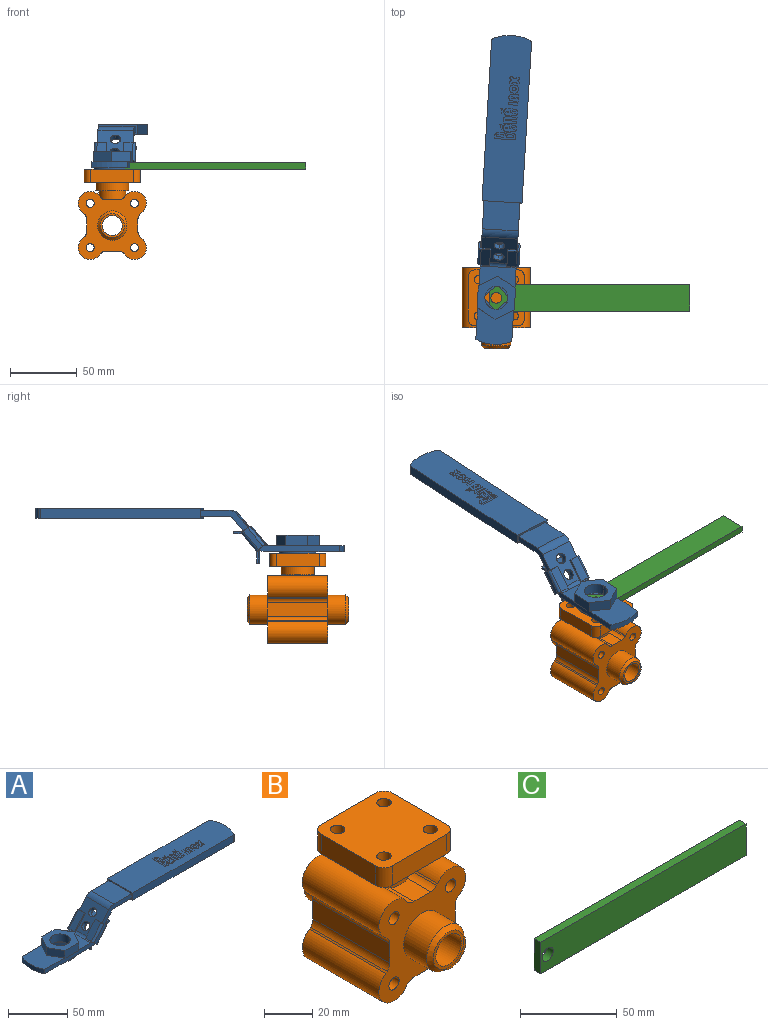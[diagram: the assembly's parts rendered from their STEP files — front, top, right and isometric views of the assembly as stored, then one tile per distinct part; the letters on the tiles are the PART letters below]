
ASSEMBLY  parts=3 mates=2
PART A: 211 faces, bbox 232x31x41.1 mm
  f0: plane 1.5x0.5mm, normal (-0.95,-0.32,0), area 0.2mm2, adj f1,f2,f4,f5
  f1: plane 125x30mm, normal (0,0,1), area 3406.6mm2, adj f0,f2,f3,f4,f6,f7,f8,f9
  f2: plane 3x0.5mm, normal (-0.16,0.99,0), area 0.3mm2, adj f0,f1,f3,f5
  f3: plane 1x0.5mm, normal (0.89,0.45,0), area 0.1mm2, adj f1,f2,f4,f5
  f4: plane 3x1mm, normal (0.32,-0.95,0), area 0.3mm2, adj f0,f1,f3,f5
  f5: plane 3.5x2mm, normal (0,0,1), area 4.1mm2, adj f0,f2,f3,f4
  f6: plane 3x0.5mm, normal (-0.16,0.99,0), area 0.3mm2, adj f1,f7,f9,f10
  f7: plane 1x0.5mm, normal (0.89,0.45,0), area 0.1mm2, adj f1,f6,f8,f10
  f8: plane 3x1mm, normal (0.32,-0.95,0), area 0.3mm2, adj f1,f7,f9,f10
  f9: plane 1.5x0.5mm, normal (-0.95,-0.32,0), area 0.2mm2, adj f1,f6,f8,f10
  f10: plane 3.5x2mm, normal (0,0,1), area 4.1mm2, adj f6,f7,f8,f9
  f11: cylinder r=3.04mm len=6mm, axis (0,0,1), area 0.9mm2, adj f1,f12,f14,f15
  f12: plane 1.86x0.1mm, normal (1,0,0), area 0.2mm2, adj f1,f11,f13,f15
  f13: cylinder r=3.04mm len=6mm, axis (0,0,1), area 0.9mm2, adj f1,f12,f14,f15
  f14: plane 1.86x0.1mm, normal (-1,0,0), area 0.2mm2, adj f1,f11,f13,f15
  f15: plane 7x6mm, normal (0,0,1), area 28.3mm2, adj f11,f12,f13,f14,f16,f17,f18,f19
  f16: plane 0.92x0.1mm, normal (-1,0,0), area 0.1mm2, adj f15,f17,f19,f20
  f17: cylinder r=1.27mm len=2.5mm, axis (0,0,1), area 0.4mm2, adj f15,f16,f18,f20
  f18: plane 0.92x0.1mm, normal (1,0,0), area 0.1mm2, adj f15,f17,f19,f20
  f19: cylinder r=1.27mm len=2.5mm, axis (0,0,1), area 0.4mm2, adj f15,f16,f18,f20
  f20: plane 3x2.5mm, normal (0,0,1), area 6.2mm2, adj f16,f17,f18,f19
  f21: plane 2x0.1mm, normal (0,1,0), area 0.2mm2, adj f1,f22,f30,f31
  f22: plane 4.7x0.1mm, normal (1,0,0), area 0.5mm2, adj f1,f21,f23,f31
  f23: cylinder r=2.3mm len=2.3mm, axis (0,0,1), area 0.4mm2, adj f1,f22,f24,f31
  f24: plane 0.4x0.1mm, normal (0,-1,0), area 0mm2, adj f1,f23,f25,f31
  f25: cylinder r=2.3mm len=2.3mm, axis (0,0,1), area 0.4mm2, adj f1,f24,f26,f31
  f26: plane 4.7x0.1mm, normal (-1,0,0), area 0.5mm2, adj f1,f25,f27,f31
  f27: plane 2x0.1mm, normal (0,1,0), area 0.2mm2, adj f1,f26,f28,f31
  f28: plane 5x0.1mm, normal (1,0,0), area 0.5mm2, adj f1,f27,f29,f31
  f29: plane 1x0.1mm, normal (0,1,0), area 0.1mm2, adj f1,f28,f30,f31
  f30: plane 5x0.1mm, normal (-1,0,0), area 0.5mm2, adj f1,f21,f29,f31
  f31: plane 7x5mm, normal (0,0,1), area 27.7mm2, adj f21,f22,f23,f24,f25,f26,f27,f28
  f32: plane 2x0.1mm, normal (0,1,0), area 0.2mm2, adj f1,f33,f35,f36
  f33: plane 7x0.1mm, normal (1,0,0), area 0.7mm2, adj f1,f32,f34,f36
  f34: plane 2x0.1mm, normal (0,-1,0), area 0.2mm2, adj f1,f33,f35,f36
  f35: plane 7x0.1mm, normal (-1,0,0), area 0.7mm2, adj f1,f32,f34,f36
  f36: plane 7x2mm, normal (0,0,1), area 14mm2, adj f32,f33,f34,f35
  f37: plane 2x0.1mm, normal (0,1,0), area 0.2mm2, adj f1,f38,f46,f47
  f38: plane 10x0.1mm, normal (1,0,0), area 1mm2, adj f1,f37,f39,f47
  f39: plane 2x0.1mm, normal (0,-1,0), area 0.2mm2, adj f1,f38,f40,f47
  f40: plane 0.27x0.1mm, normal (-1,0,0), area 0mm2, adj f1,f39,f41,f47
  f41: cylinder r=2mm len=3mm, axis (0,0,1), area 0.4mm2, adj f1,f40,f42,f47
  f42: plane 8x0.1mm, normal (-1,0,0), area 0.8mm2, adj f1,f41,f43,f47
  f43: plane 2x0.1mm, normal (0,1,0), area 0.2mm2, adj f1,f42,f44,f47
  f44: plane 8.5x0.1mm, normal (1,0,0), area 0.9mm2, adj f1,f43,f45,f47
  f45: plane 1x0.1mm, normal (0,1,0), area 0.1mm2, adj f1,f44,f46,f47
  f46: plane 8.5x0.1mm, normal (-1,0,0), area 0.9mm2, adj f1,f37,f45,f47
  f47: plane 10x5mm, normal (0,0,1), area 40.6mm2, adj f37,f38,f39,f40,f41,f42,f43,f44
  f48: cylinder r=2mm len=7.5mm, axis (0,0,1), area 17.3mm2, adj f1,f49,f134,f135
  f49: cylinder r=33.89mm len=27.63mm, axis (0,0,1), area 213.4mm2, adj f1,f48,f50,f135
  f50: cylinder r=2mm len=7.5mm, axis (0,0,1), area 17.3mm2, adj f1,f49,f51,f135
  f51: plane 120.23x7.5mm, normal (0,-1,0), area 901.7mm2, adj f1,f50,f52,f135
  f52: plane 30x7.5mm, normal (-1,0,0), area 103.5mm2, adj f1,f51,f53,f81,f105,f123,f134,f135
  f53: plane 104.03x31mm, normal (0,-1,0), area 520.7mm2, adj f52,f54,f56,f58,f59,f82,f100,f101
  f54: plane 27x22.22mm, normal (-0.77,0,0.64), area 671.8mm2, adj f53,f55,f56,f57,f58,f80,f81,f106
  f55: plane 14.49x12.72mm, normal (0,-1,0), area 26.8mm2, adj f54,f56,f59,f72,f80,f127
  f56: cylinder r=4mm len=27mm, axis (0,-1,0), area 68.6mm2, adj f53,f54,f55,f57,f59,f81,f82
  f57: plane 14.49x12.72mm, normal (0,1,0), area 26.8mm2, adj f54,f56,f58,f59,f72,f76
  f58: plane 13.79x11.57mm, normal (0.77,0,-0.64), area 117.3mm2, adj f53,f54,f57,f59,f72,f77
  f59: plane 31x6.13mm, normal (-0.64,0,-0.77), area 59.9mm2, adj f53,f55,f56,f57,f58,f60,f61,f65
  f60: cylinder r=3mm len=15mm, axis (0,-1,0), area 14.6mm2, adj f59,f61,f64,f65
  f61: plane 9.88x1.85mm, normal (0,-1,0), area 14.2mm2, adj f59,f60,f62,f63,f64,f66,f67
  f62: plane 15x8.91mm, normal (1,0,0), area 133.7mm2, adj f61,f63,f65,f66
  f63: plane 15x1.5mm, normal (0,0,-1), area 22.5mm2, adj f61,f62,f64,f65
  f64: plane 15x8.91mm, normal (-1,0,0), area 133.7mm2, adj f60,f61,f63,f65
  f65: plane 9.88x1.85mm, normal (0,1,0), area 14.2mm2, adj f59,f60,f62,f63,f64,f66,f67
  f66: cylinder r=1.5mm len=15mm, axis (0,-1,0), area 15.7mm2, adj f61,f62,f65,f67
  f67: plane 27x13.79mm, normal (0.77,0,-0.64), area 371.7mm2, adj f59,f61,f65,f66,f68,f70,f72,f73
  f68: cylinder r=1.5mm len=24.5mm, axis (0,-1,0), area 32.1mm2, adj f67,f69,f70,f131
  f69: plane 24.5x5.6mm, normal (0,0,-1), area 137.3mm2, adj f68,f70,f131,f132
  f70: plane 6.75x2.04mm, normal (0,-1,0), area 9.4mm2, adj f67,f68,f69,f71,f72,f132,f133
  f71: cylinder r=3mm len=24.5mm, axis (0,-1,0), area 28.5mm2, adj f70,f72,f131,f133
  f72: plane 31x6.13mm, normal (0.64,0,0.77), area 56.8mm2, adj f55,f57,f58,f67,f70,f71,f73,f74
  f73: cylinder r=2mm len=15.07mm, axis (0.64,0,0.77), area 56.5mm2, adj f59,f67,f72,f74
  f74: plane 16.36x14.63mm, normal (0,-1,0), area 72mm2, adj f59,f72,f73,f75
  f75: cylinder r=2mm len=15.07mm, axis (0.64,0,0.77), area 56.5mm2, adj f59,f72,f74,f76
  f76: plane 13.79x11.57mm, normal (-0.77,0,0.64), area 126mm2, adj f57,f59,f72,f75
  f77: plane 17x15.4mm, normal (0,1,0), area 90mm2, adj f58,f59,f72,f78
  f78: plane 28x13.79mm, normal (-0.77,0,0.64), area 440.4mm2, adj f59,f72,f77,f79,f125,f126
  f79: plane 17x15.4mm, normal (0,-1,0), area 90mm2, adj f59,f72,f78,f80
  f80: plane 13.79x11.57mm, normal (0.77,0,-0.64), area 117.3mm2, adj f54,f55,f59,f72,f79,f81
  f81: plane 104.03x31mm, normal (0,1,0), area 520.7mm2, adj f52,f54,f56,f59,f80,f82,f101,f102
  f82: plane 27x14.76mm, normal (0,0,1), area 293.3mm2, adj f53,f56,f81,f83,f84
  f83: plane 14x8.08mm, normal (0.87,0.5,0), area 129.3mm2, adj f82,f84,f88,f89,f121
  f84: plane 14x8.08mm, normal (0.87,-0.5,0), area 129.3mm2, adj f82,f83,f85,f89,f122
  f85: plane 16.17x8mm, normal (0,-1,0), area 129.3mm2, adj f84,f86,f89,f122
  f86: plane 14x8.08mm, normal (-0.87,-0.5,0), area 129.3mm2, adj f85,f87,f89,f113,f122
  f87: plane 14x8.08mm, normal (-0.87,0.5,0), area 129.3mm2, adj f86,f88,f89,f113,f121
  f88: plane 16.17x8mm, normal (0,1,0), area 129.3mm2, adj f83,f87,f89,f121
  f89: plane 32.33x28mm, normal (0,0,1), area 444.2mm2, adj f83,f84,f85,f86,f87,f88,f90,f91
  f90: cylinder r=8.64mm len=17.18mm, axis (0,0,1), area 217.3mm2, adj f89,f91,f114,f115,f117,f118
  f91: cylinder r=8.64mm len=17.18mm, axis (0,0,1), area 217.3mm2, adj f89,f90,f92,f116,f119,f120
  f92: plane 2.73x1.36mm, normal (0,0,-1), area 1.7mm2, adj f91,f93,f94
  f93: plane 9.9x9.9mm, normal (-0.71,-0.71,0), area 77mm2, adj f92,f94,f96,f97,f116,f120
  f94: plane 9.9x9.9mm, normal (-0.71,0.71,0), area 77mm2, adj f92,f93,f95,f97,f117,f119
  f95: plane 9.9x9.9mm, normal (0.71,0.71,0), area 77mm2, adj f94,f96,f97,f114,f117,f118
  f96: plane 9.9x9.9mm, normal (0.71,-0.71,0), area 77mm2, adj f93,f95,f97,f114,f115,f116
  f97: plane 28x28mm, normal (0,0,-1), area 419.8mm2, adj f93,f94,f95,f96,f98,f99
  f98: cylinder r=14mm len=28mm, axis (0,0,1), area 44mm2, adj f97,f99,f100,f110,f111
  f99: cylinder r=14mm len=28mm, axis (0,0,1), area 44mm2, adj f97,f98,f100,f101,f110
  f100: plane 7.42x0.5mm, normal (0,0,1), area 2.5mm2, adj f53,f98,f99
  f101: plane 27x19.66mm, normal (0,0,-1), area 325.6mm2, adj f53,f81,f99,f102
  f102: cylinder r=8mm len=27mm, axis (0,-1,0), area 188.5mm2, adj f53,f81,f101,f103
  f103: plane 27x22.21mm, normal (0.77,0,-0.64), area 682.4mm2, adj f53,f81,f102,f104,f106,f107,f108,f109
  f104: cylinder r=4mm len=27mm, axis (0,-1,0), area 94.3mm2, adj f53,f81,f103,f105
  f105: plane 27x20.82mm, normal (0,0,-1), area 562.1mm2, adj f52,f53,f81,f104
  f106: cylinder r=4mm len=9.02mm, axis (-0.77,0,0.64), area 56.6mm2, adj f54,f103,f107
  f107: cylinder r=4mm len=9.02mm, axis (-0.77,0,0.64), area 56.6mm2, adj f54,f103,f106
  f108: cylinder r=4mm len=9.02mm, axis (-0.77,0,0.64), area 56.5mm2, adj f54,f103,f109
  f109: cylinder r=4mm len=9.02mm, axis (-0.77,0,0.64), area 56.5mm2, adj f54,f103,f108
  f110: plane 7.42x0.5mm, normal (0,0,1), area 2.5mm2, adj f81,f98,f99
  f111: plane 31.3x27mm, normal (0,0,-1), area 613.4mm2, adj f53,f81,f98,f112
  f112: cylinder r=31.88mm len=27mm, axis (0,0,1), area 125.5mm2, adj f53,f81,f111,f113
  f113: plane 27x26.64mm, normal (0,0,1), area 587.5mm2, adj f53,f81,f86,f87,f112
  f114: plane 2.73x1.36mm, normal (0,0,-1), area 1.7mm2, adj f90,f95,f96
  f115: plane 7.17x7.17mm, normal (0,0,1), area 11.4mm2, adj f90,f96
  f116: plane 2.73x1.36mm, normal (0,0,-1), area 1.7mm2, adj f91,f93,f96
  f117: plane 2.73x1.36mm, normal (0,0,-1), area 1.7mm2, adj f90,f94,f95
  f118: plane 7.17x7.17mm, normal (0,0,1), area 11.4mm2, adj f90,f95
  f119: plane 7.17x7.17mm, normal (0,0,1), area 11.4mm2, adj f91,f94
  f120: plane 7.17x7.17mm, normal (0,0,1), area 11.4mm2, adj f91,f93
  f121: plane 16.74x0.5mm, normal (0,0,-1), area 8.2mm2, adj f81,f83,f87,f88
  f122: plane 16.74x0.5mm, normal (0,0,-1), area 8.2mm2, adj f53,f84,f85,f86
  f123: plane 27x21.05mm, normal (0,0,1), area 568.3mm2, adj f52,f53,f81,f124
  f124: cylinder r=8mm len=27mm, axis (0,-1,0), area 188.4mm2, adj f53,f54,f81,f123
  f125: cylinder r=4.5mm len=7.86mm, axis (-0.77,0,0.64), area 21.2mm2, adj f67,f78,f126
  f126: cylinder r=4.5mm len=7.86mm, axis (-0.77,0,0.64), area 21.2mm2, adj f67,f78,f125
  f127: plane 13.79x11.57mm, normal (-0.77,0,0.64), area 126mm2, adj f55,f59,f72,f128
  f128: cylinder r=2mm len=15.07mm, axis (0.64,0,0.77), area 56.5mm2, adj f59,f72,f127,f129
  f129: plane 16.36x14.63mm, normal (0,1,0), area 72mm2, adj f59,f72,f128,f130
  f130: cylinder r=2mm len=15.07mm, axis (0.64,0,0.77), area 56.5mm2, adj f59,f67,f72,f129
  f131: plane 6.75x2.04mm, normal (0,1,0), area 9.4mm2, adj f67,f68,f69,f71,f72,f132,f133
  f132: plane 24.5x1.5mm, normal (1,0,0), area 36.7mm2, adj f69,f70,f131,f133
  f133: plane 24.5x5.6mm, normal (0,0,1), area 137.3mm2, adj f70,f71,f131,f132
  f134: plane 120.23x7.5mm, normal (0,1,0), area 901.7mm2, adj f1,f48,f52,f135
  f135: plane 125x30mm, normal (0,0,-1), area 3715.2mm2, adj f48,f49,f50,f51,f52,f134
  f136: plane 2x0.1mm, normal (0,1,0), area 0.2mm2, adj f1,f137,f144,f145
  f137: plane 16x0.1mm, normal (1,0,0), area 1.6mm2, adj f1,f136,f138,f145
  f138: plane 2x0.1mm, normal (0,-1,0), area 0.2mm2, adj f1,f137,f139,f145
  f139: cylinder r=3mm len=3mm, axis (0,0,1), area 0.5mm2, adj f1,f138,f140,f145
  f140: plane 3x0.1mm, normal (-1,0,0), area 0.3mm2, adj f1,f139,f141,f145
  f141: cylinder r=2mm len=2mm, axis (0,0,1), area 0.3mm2, adj f1,f140,f142,f145
  f142: cylinder r=2mm len=2mm, axis (0,0,1), area 0.3mm2, adj f1,f141,f143,f145
  f143: plane 3x0.1mm, normal (-1,0,0), area 0.3mm2, adj f1,f142,f144,f145
  f144: cylinder r=3mm len=3mm, axis (0,0,1), area 0.5mm2, adj f1,f136,f143,f145
  f145: plane 16x5mm, normal (0,0,1), area 53.8mm2, adj f136,f137,f138,f139,f140,f141,f142,f143
  f146: plane 1x0.1mm, normal (0,-1,0), area 0.1mm2, adj f145,f147,f151,f152
  f147: cylinder r=1mm len=1mm, axis (0,0,1), area 0.2mm2, adj f145,f146,f148,f152
  f148: plane 3x0.1mm, normal (1,0,0), area 0.3mm2, adj f145,f147,f149,f152
  f149: cylinder r=1.5mm len=1.5mm, axis (0,0,1), area 0.2mm2, adj f145,f148,f150,f152
  f150: plane 0.5x0.1mm, normal (0,1,0), area 0.1mm2, adj f145,f149,f151,f152
  f151: plane 5.5x0.1mm, normal (-1,0,0), area 0.6mm2, adj f145,f146,f150,f152
  f152: plane 5.5x2mm, normal (0,0,1), area 10.3mm2, adj f146,f147,f148,f149,f150,f151
  f153: plane 5.5x0.1mm, normal (-1,0,0), area 0.6mm2, adj f145,f154,f158,f159
  f154: plane 0.5x0.1mm, normal (0,-1,0), area 0.1mm2, adj f145,f153,f155,f159
  f155: cylinder r=1.5mm len=1.5mm, axis (0,0,1), area 0.2mm2, adj f145,f154,f156,f159
  f156: plane 3x0.1mm, normal (1,0,0), area 0.3mm2, adj f145,f155,f157,f159
  f157: cylinder r=1mm len=1mm, axis (0,0,1), area 0.2mm2, adj f145,f156,f158,f159
  f158: plane 1x0.1mm, normal (0,1,0), area 0.1mm2, adj f145,f153,f157,f159
  f159: plane 5.5x2mm, normal (0,0,1), area 10.3mm2, adj f153,f154,f155,f156,f157,f158
  f160: plane 1x0.1mm, normal (0,1,0), area 0.1mm2, adj f1,f161,f173,f174
  f161: cylinder r=2mm len=2mm, axis (0,0,1), area 0.3mm2, adj f1,f160,f162,f174
  f162: plane 6x0.1mm, normal (1,0,0), area 0.6mm2, adj f1,f161,f163,f174
  f163: cylinder r=2mm len=2mm, axis (0,0,1), area 0.3mm2, adj f1,f162,f164,f174
  f164: plane 1x0.1mm, normal (0,-1,0), area 0.1mm2, adj f1,f163,f165,f174
  f165: cylinder r=2mm len=2mm, axis (0,0,1), area 0.3mm2, adj f1,f164,f166,f174
  f166: plane 3x0.1mm, normal (-1,0,0), area 0.3mm2, adj f1,f165,f167,f174
  f167: plane 3x0.1mm, normal (0,1,0), area 0.3mm2, adj f1,f166,f168,f174
  f168: plane 3.5x0.1mm, normal (-1,0,0), area 0.4mm2, adj f1,f167,f169,f174
  f169: plane 1x0.1mm, normal (0,-1,0), area 0.1mm2, adj f1,f168,f170,f174
  f170: plane 2.5x0.1mm, normal (1,0,0), area 0.3mm2, adj f1,f169,f171,f174
  f171: plane 2x0.1mm, normal (0,-1,0), area 0.2mm2, adj f1,f170,f172,f174
  f172: plane 2x0.1mm, normal (-1,0,0), area 0.2mm2, adj f1,f171,f173,f174
  f173: cylinder r=2mm len=2mm, axis (0,0,1), area 0.3mm2, adj f1,f160,f172,f174
  f174: plane 10x5mm, normal (0,0,1), area 39.1mm2, adj f160,f161,f162,f163,f164,f165,f166,f167
  f175: plane 2x0.1mm, normal (-1,0,0), area 0.2mm2, adj f174,f176,f178,f179
  f176: plane 1x0.1mm, normal (0,-1,0), area 0.1mm2, adj f174,f175,f177,f179
  f177: plane 2x0.1mm, normal (1,0,0), area 0.2mm2, adj f174,f176,f178,f179
  f178: plane 1x0.1mm, normal (0,1,0), area 0.1mm2, adj f174,f175,f177,f179
  f179: plane 2x1mm, normal (0,0,1), area 2mm2, adj f175,f176,f177,f178
  f180: plane 1x0.1mm, normal (0,1,0), area 0.1mm2, adj f1,f181,f193,f194
  f181: cylinder r=2mm len=2mm, axis (0,0,1), area 0.3mm2, adj f1,f180,f182,f194
  f182: plane 6x0.1mm, normal (1,0,0), area 0.6mm2, adj f1,f181,f183,f194
  f183: cylinder r=2mm len=2mm, axis (0,0,1), area 0.3mm2, adj f1,f182,f184,f194
  f184: plane 1x0.1mm, normal (0,-1,0), area 0.1mm2, adj f1,f183,f185,f194
  f185: cylinder r=2mm len=2mm, axis (0,0,1), area 0.3mm2, adj f1,f184,f186,f194
  f186: plane 3x0.1mm, normal (-1,0,0), area 0.3mm2, adj f1,f185,f187,f194
  f187: plane 3x0.1mm, normal (0,1,0), area 0.3mm2, adj f1,f186,f188,f194
  f188: plane 3.5x0.1mm, normal (-1,0,0), area 0.4mm2, adj f1,f187,f189,f194
  f189: plane 1x0.1mm, normal (0,-1,0), area 0.1mm2, adj f1,f188,f190,f194
  f190: plane 2.5x0.1mm, normal (1,0,0), area 0.3mm2, adj f1,f189,f191,f194
  f191: plane 2x0.1mm, normal (0,-1,0), area 0.2mm2, adj f1,f190,f192,f194
  f192: plane 2x0.1mm, normal (-1,0,0), area 0.2mm2, adj f1,f191,f193,f194
  f193: cylinder r=2mm len=2mm, axis (0,0,1), area 0.3mm2, adj f1,f180,f192,f194
  f194: plane 10x5mm, normal (0,0,1), area 39.1mm2, adj f180,f181,f182,f183,f184,f185,f186,f187
  f195: plane 2x0.1mm, normal (-1,0,0), area 0.2mm2, adj f194,f196,f198,f199
  f196: plane 1x0.1mm, normal (0,-1,0), area 0.1mm2, adj f194,f195,f197,f199
  f197: plane 2x0.1mm, normal (1,0,0), area 0.2mm2, adj f194,f196,f198,f199
  f198: plane 1x0.1mm, normal (0,1,0), area 0.1mm2, adj f194,f195,f197,f199
  f199: plane 2x1mm, normal (0,0,1), area 2mm2, adj f195,f196,f197,f198
  f200: plane 2x0.1mm, normal (1,0,0), area 0.2mm2, adj f1,f201,f209,f210
  f201: cylinder r=1.53mm len=3mm, axis (0,0,1), area 0.4mm2, adj f1,f200,f202,f210
  f202: plane 2.01x0.1mm, normal (1,0,0), area 0.2mm2, adj f1,f201,f203,f210
  f203: cylinder r=1.99mm len=2.5mm, axis (0,0,1), area 0.3mm2, adj f1,f202,f204,f210
  f204: cylinder r=1.99mm len=2.5mm, axis (0,0,1), area 0.3mm2, adj f1,f203,f205,f210
  f205: plane 2.01x0.1mm, normal (-1,0,0), area 0.2mm2, adj f1,f204,f206,f210
  f206: cylinder r=1.53mm len=3mm, axis (0,0,1), area 0.4mm2, adj f1,f205,f207,f210
  f207: plane 2x0.1mm, normal (-1,0,0), area 0.2mm2, adj f1,f206,f208,f210
  f208: cylinder r=1.99mm len=2.5mm, axis (0,0,1), area 0.3mm2, adj f1,f207,f209,f210
  f209: cylinder r=1.99mm len=2.5mm, axis (0,0,1), area 0.3mm2, adj f1,f200,f208,f210
  f210: plane 7.16x5mm, normal (0,0,1), area 27mm2, adj f200,f201,f202,f203,f204,f205,f206,f207
PART B: 59 faces, bbox 51x76x67.8 mm
  f0: plane 18.39x0.67mm, normal (0.71,0,0.71), area 15.9mm2, adj f1,f9,f28,f42
  f1: cylinder r=8.88mm len=45mm, axis (0,1,0), area 1425.9mm2, adj f0,f10,f11,f27,f28,f42
  f2: cylinder r=8.88mm len=45mm, axis (0,1,0), area 1425.9mm2, adj f3,f21,f22,f27,f28,f42
  f3: plane 18.39x0.67mm, normal (-0.71,0,0.71), area 15.9mm2, adj f2,f6,f28,f42
  f4: plane 13.8x9.86mm, normal (0,0,1), area 127.4mm2, adj f6,f9,f28,f42
  f5: plane 13.8x9.86mm, normal (0,0,1), area 127.4mm2, adj f7,f8,f27,f42
  f6: cylinder r=5mm len=17.18mm, axis (0,-1,0), area 60.1mm2, adj f3,f4,f28,f42
  f7: cylinder r=5mm len=17.18mm, axis (0,-1,0), area 60.1mm2, adj f5,f22,f27,f42
  f8: cylinder r=5mm len=17.18mm, axis (0,1,0), area 60.1mm2, adj f5,f10,f27,f42
  f9: cylinder r=5mm len=17.18mm, axis (0,1,0), area 60.1mm2, adj f0,f4,f28,f42
  f10: plane 18.39x0.67mm, normal (0.71,0,0.71), area 15.9mm2, adj f1,f8,f27,f42
  f11: plane 45x0.64mm, normal (-0.71,0,-0.71), area 40.4mm2, adj f1,f27,f28,f29
  f12: plane 45x9.86mm, normal (-1,0,0), area 443.6mm2, adj f27,f28,f29,f30
  f13: plane 45x0.64mm, normal (-0.71,0,0.71), area 40.4mm2, adj f14,f27,f28,f30
  f14: cylinder r=8.88mm len=45mm, axis (0,1,0), area 1434.5mm2, adj f13,f15,f27,f28
  f15: plane 45x0.64mm, normal (0.71,0,-0.71), area 40.4mm2, adj f14,f27,f28,f31
  f16: plane 45x9.86mm, normal (0,0,-1), area 443.6mm2, adj f27,f28,f31,f32
  f17: plane 45x0.64mm, normal (-0.71,0,-0.71), area 40.4mm2, adj f18,f27,f28,f32
  f18: cylinder r=8.88mm len=45mm, axis (0,1,0), area 1434.5mm2, adj f17,f19,f27,f28
  f19: plane 45x0.64mm, normal (0.71,0,0.71), area 40.4mm2, adj f18,f27,f28,f33
  f20: plane 45x9.86mm, normal (1,0,0), area 443.6mm2, adj f27,f28,f33,f34
  f21: plane 45x0.64mm, normal (0.71,0,-0.71), area 40.4mm2, adj f2,f27,f28,f34
  f22: plane 18.39x0.67mm, normal (-0.71,0,0.71), area 15.9mm2, adj f2,f7,f27,f42
  f23: cylinder r=3mm len=45mm, axis (0,1,0), area 848.2mm2, adj f27,f28
  f24: cylinder r=3mm len=45mm, axis (0,1,0), area 848.2mm2, adj f27,f28
  f25: cylinder r=3mm len=45mm, axis (0,1,0), area 848.2mm2, adj f27,f28
  f26: cylinder r=3mm len=45mm, axis (0,1,0), area 848.2mm2, adj f27,f28
  f27: plane 51x51mm, normal (0,-1,0), area 1533.5mm2, adj f1,f2,f5,f7,f8,f10,f11,f12
  f28: plane 51x51mm, normal (0,1,0), area 1533.5mm2, adj f0,f1,f2,f3,f4,f6,f9,f11
  f29: cylinder r=5mm len=45mm, axis (0,1,0), area 176.7mm2, adj f11,f12,f27,f28
  f30: cylinder r=5mm len=45mm, axis (0,-1,0), area 176.7mm2, adj f12,f13,f27,f28
  f31: cylinder r=5mm len=45mm, axis (0,1,0), area 176.7mm2, adj f15,f16,f27,f28
  f32: cylinder r=5mm len=45mm, axis (0,-1,0), area 176.7mm2, adj f16,f17,f27,f28
  f33: cylinder r=5mm len=45mm, axis (0,-1,0), area 176.7mm2, adj f19,f20,f27,f28
  f34: cylinder r=5mm len=45mm, axis (0,1,0), area 176.7mm2, adj f20,f21,f27,f28
  f35: plane 18x18mm, normal (0,1,0), area 77.8mm2, adj f37,f40
  f36: cylinder r=11mm len=22mm, axis (0,1,0), area 933.1mm2, adj f28,f40
  f37: cylinder r=7.5mm len=76mm, axis (0,1,0), area 3581.4mm2, adj f35,f39
  f38: cylinder r=11mm len=22mm, axis (0,1,0), area 933.1mm2, adj f27,f41
  f39: plane 18x18mm, normal (0,-1,0), area 77.8mm2, adj f37,f41
  f40: cone r=11mm half-angle=45deg, axis (0,-1,0), area 177.7mm2, adj f35,f36
  f41: cone r=9mm half-angle=45deg, axis (0,1,0), area 177.7mm2, adj f38,f39
  f42: cylinder r=10mm len=20mm, axis (0,0,-1), area 370.1mm2, adj f0,f1,f2,f3,f4,f5,f6,f7
  f43: cylinder r=12.5mm len=25mm, axis (0,0,-1), area 471.2mm2, adj f44,f54
  f44: plane 25x25mm, normal (0,0,-1), area 176.7mm2, adj f42,f43
  f45: plane 32x10mm, normal (1,0,0), area 320mm2, adj f53,f54,f55,f58
  f46: plane 32x10mm, normal (0,1,0), area 320mm2, adj f53,f54,f55,f56
  f47: plane 32x10mm, normal (-1,0,0), area 320mm2, adj f53,f54,f56,f57
  f48: cylinder r=3mm len=10mm, axis (0,0,-1), area 188.5mm2, adj f53,f54
  f49: cylinder r=3mm len=10mm, axis (0,0,-1), area 188.5mm2, adj f53,f54
  f50: plane 32x10mm, normal (0,-1,0), area 320mm2, adj f53,f54,f57,f58
  f51: cylinder r=3mm len=10mm, axis (0,0,-1), area 188.5mm2, adj f53,f54
  f52: cylinder r=3mm len=10mm, axis (0,0,-1), area 188.5mm2, adj f53,f54
  f53: plane 42x42mm, normal (0,0,1), area 1629.4mm2, adj f45,f46,f47,f48,f49,f50,f51,f52
  f54: plane 42x42mm, normal (0,0,-1), area 1138.6mm2, adj f43,f45,f46,f47,f48,f49,f50,f51
  f55: cylinder r=5mm len=10mm, axis (0,0,1), area 78.5mm2, adj f45,f46,f53,f54
  f56: cylinder r=5mm len=10mm, axis (0,0,-1), area 78.5mm2, adj f46,f47,f53,f54
  f57: cylinder r=5mm len=10mm, axis (0,0,1), area 78.5mm2, adj f47,f50,f53,f54
  f58: cylinder r=5mm len=10mm, axis (0,0,-1), area 78.5mm2, adj f45,f50,f53,f54
PART C: 7 faces, bbox 150x5x20 mm
  f0: plane 20x5mm, normal (-1,0,0), area 100mm2, adj f1,f3,f5,f6
  f1: plane 150x5mm, normal (0,0,-1), area 750mm2, adj f0,f2,f5,f6
  f2: plane 20x5mm, normal (1,0,0), area 100mm2, adj f1,f3,f5,f6
  f3: plane 150x5mm, normal (0,0,1), area 750mm2, adj f0,f2,f5,f6
  f4: cylinder r=4.07mm len=8.15mm, axis (0,1,0), area 128mm2, adj f5,f6
  f5: plane 150x20mm, normal (0,-1,0), area 2947.8mm2, adj f0,f1,f2,f3,f4
  f6: plane 150x20mm, normal (0,1,0), area 2947.8mm2, adj f0,f1,f2,f3,f4
PLACE A rot(axis=(0,0,1),86.6deg) t=(-47.46,15.63,50.32)mm
PLACE B t=(-47.46,15.63,7.07)mm fixed
PLACE C rot(axis=(1,0,0),90deg) t=(-52.46,25.63,54.32)mm
MATE pin_slot C.f4 <-> B.f42  axis (0,0,-1) through (-47.46,15.63,49.32)mm
MATE pin_slot A.f90 <-> B.f42  axis (0,0,-1) through (-47.46,15.63,49.32)mm
